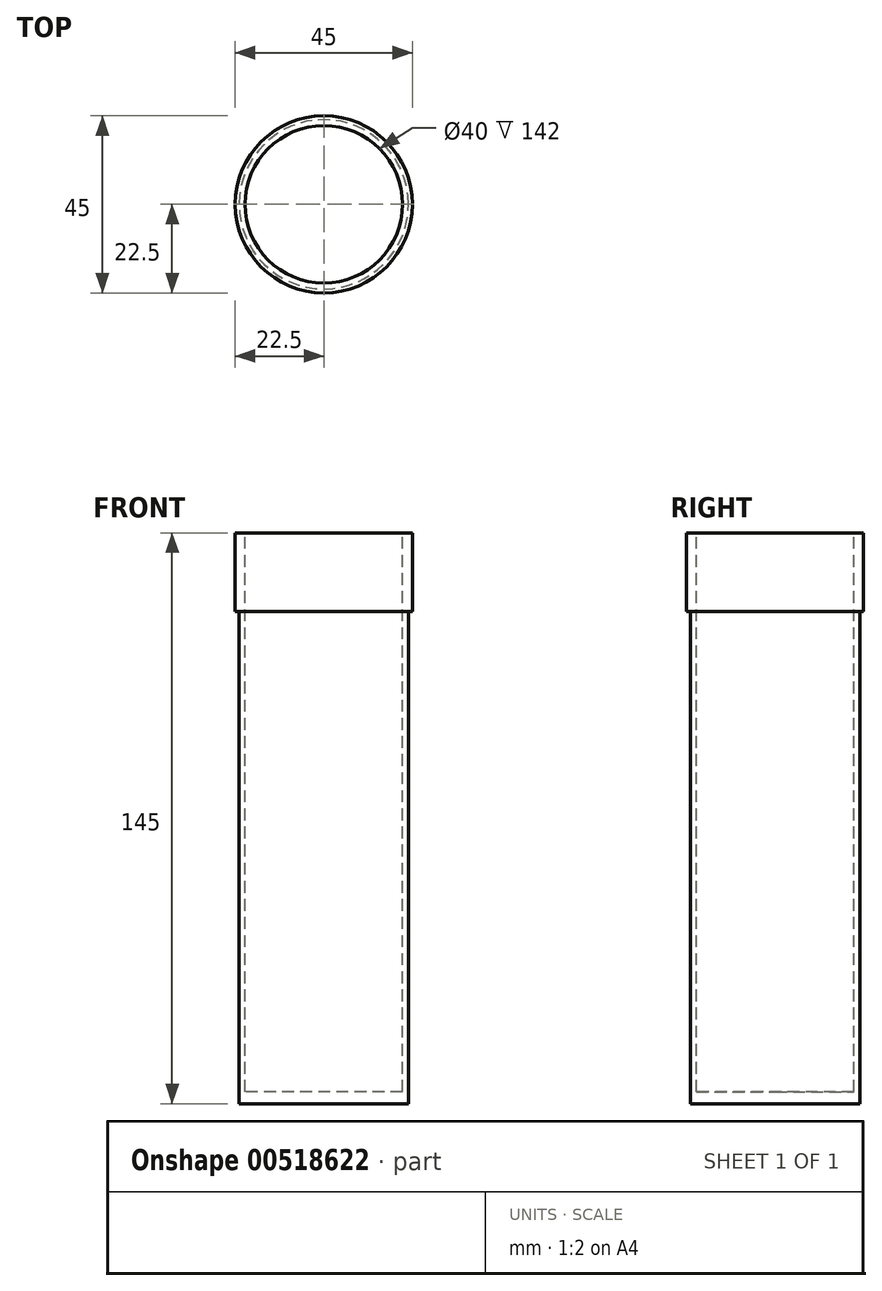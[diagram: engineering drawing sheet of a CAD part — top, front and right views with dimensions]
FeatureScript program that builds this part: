
annotation { "Feature Type Name" : "Feature", "Feature Type Description" : "" }
export const myFeature = defineFeature(function(context is Context, id is Id, definition is map)
    precondition{}
    {
        {
            var Q0;
            Q0=qCreatedBy(makeId("Top.planeOp"),FACE);
            var sketch = newSketch(context, id + "F0", { "sketchPlane" : qUnion([Q0])});
            skCircle(sketch, "E0", {"center": v(0, 0) * mm, "radius": 21.5 * mm});
            skSolve(sketch);
        }
        {
            var Q0;
            Q0 = qSketchRegion(id + "F0", true);
            extrude(context, id + "F1", {"entities" : qUnion([Q0]), "depth" : 125 * mm, "offsetDistance" : 25.4 * mm});
        }
        {
            var Q0;
            Q0=makeQuery(id+"F1.opExtrude","CAP_FACE",FACE,{"disambiguationData":[OSD([sQuery(id+"F0.wireOp",EDGE,"E0")])],"isStart":false});
            var sketch = newSketch(context, id + "F2", { "sketchPlane" : qUnion([Q0])});
            skCircle(sketch, "E1", {"center": v(0, 0) * mm, "radius": 22.5 * mm});
            skSolve(sketch);
        }
        {
            var Q0;
            Q0 = qSketchRegion(id + "F2", true);
            extrude(context, id + "F3", {"entities" : qUnion([Q0]), "operationType" : NewBodyOperationType.ADD, "depth" : 20 * mm, "offsetDistance" : 25.4 * mm});
        }
        {
            var Q0;
            Q0=makeQuery(id+"F3.opExtrude","CAP_FACE",FACE,{"disambiguationData":[OSD([sQuery(id+"F2.wireOp",EDGE,"E1")])],"isStart":false});
            var sketch = newSketch(context, id + "F4", { "sketchPlane" : qUnion([Q0])});
            skCircle(sketch, "E2", {"center": v(0, 0) * mm, "radius": 20 * mm});
            skSolve(sketch);
        }
        {
            var Q0;
            Q0 = qSketchRegion(id + "F4", true);
            extrude(context, id + "F5", {"entities" : qUnion([Q0]), "operationType" : NewBodyOperationType.REMOVE, "oppositeDirection" : true, "depth" : 142 * mm, "offsetDistance" : 25.4 * mm});
        }
    });
